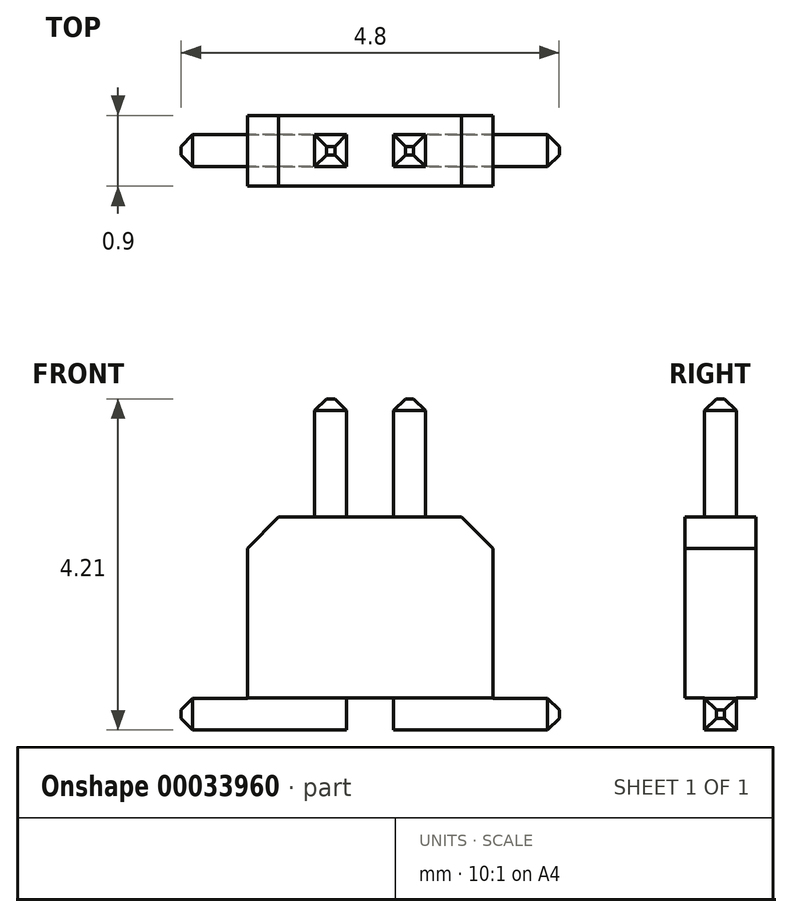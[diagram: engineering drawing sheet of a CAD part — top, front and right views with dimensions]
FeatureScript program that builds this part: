
annotation { "Feature Type Name" : "Feature", "Feature Type Description" : "" }
export const myFeature = defineFeature(function(context is Context, id is Id, definition is map)
    precondition{}
    {
        {
            var Q0;
            Q0=qCreatedBy(makeId("Top.planeOp"),FACE);
            var sketch = newSketch(context, id + "F0", { "sketchPlane" : qUnion([Q0])});
            skLineSegment(sketch, "E0.rect.bottom", {"start": v(-1.56, 0.45) * mm, "end": v(1.56, 0.45) * mm});
            skLineSegment(sketch, "E0.rect.top", {"start": v(-1.56, -0.45) * mm, "end": v(1.56, -0.45) * mm});
            skLineSegment(sketch, "E0.rect.left", {"start": v(-1.56, 0.45) * mm, "end": v(-1.56, -0.45) * mm});
            skLineSegment(sketch, "E0.rect.right", {"start": v(1.56, 0.45) * mm, "end": v(1.56, -0.45) * mm});
            skPoint(sketch, "E0.rect.middle", {"position": v(0, 0) * mm});
            skSolve(sketch);
        }
        {
            var Q0;
            Q0 = qSketchRegion(id + "F0", true);
            extrude(context, id + "F1", {"entities" : qUnion([Q0]), "depth" : 2.3 * mm});
        }
        {
            var Q0;
            Q0=makeQuery(id+"F1.opExtrude","CAP_FACE",FACE,{"disambiguationData":[OSD([sQuery(id+"F0.wireOp",EDGE,"E0.rect.bottom"),sQuery(id+"F0.wireOp",EDGE,"E0.rect.top"),sQuery(id+"F0.wireOp",EDGE,"E0.rect.left"),sQuery(id+"F0.wireOp",EDGE,"E0.rect.right")])],"isStart":false});
            var sketch = newSketch(context, id + "F2", { "sketchPlane" : qUnion([Q0])});
            skLineSegment(sketch, "E1.rect.bottom", {"start": v(-0.7, -0.2) * mm, "end": v(-0.3, -0.2) * mm});
            skLineSegment(sketch, "E1.rect.top", {"start": v(-0.7, 0.2) * mm, "end": v(-0.3, 0.2) * mm});
            skLineSegment(sketch, "E1.rect.left", {"start": v(-0.7, -0.2) * mm, "end": v(-0.7, 0.2) * mm});
            skLineSegment(sketch, "E1.rect.right", {"start": v(-0.3, -0.2) * mm, "end": v(-0.3, 0.2) * mm});
            skPoint(sketch, "E1.rect.middle", {"position": v(-0.5, 0) * mm});
            skLineSegment(sketch, "E2.rect.bottom", {"start": v(0.7, 0.2) * mm, "end": v(0.3, 0.2) * mm});
            skLineSegment(sketch, "E2.rect.top", {"start": v(0.7, -0.2) * mm, "end": v(0.3, -0.2) * mm});
            skLineSegment(sketch, "E2.rect.left", {"start": v(0.7, 0.2) * mm, "end": v(0.7, -0.2) * mm});
            skLineSegment(sketch, "E2.rect.right", {"start": v(0.3, 0.2) * mm, "end": v(0.3, -0.2) * mm});
            skPoint(sketch, "E2.rect.middle", {"position": v(0.5, 0) * mm});
            skSolve(sketch);
        }
        {
            var Q0;
            Q0 = qSketchRegion(id + "F2", true);
            extrude(context, id + "F3", {"entities" : qUnion([Q0]), "operationType" : NewBodyOperationType.ADD, "depth" : 1.5 * mm, "hasSecondDirection" : true, "secondDirectionOppositeDirection" : true, "secondDirectionDepth" : 2.7 * mm});
        }
        {
            var Q0;
            {var subQ0=sQuery(id+"F2.wireOp",EDGE,"E1.rect.left");Q0=makeQuery(id+"F3.boolean.opBoolean","SPLIT",FACE,{"disambiguationData":[TD([makeQuery(id+"F1.opExtrude","CAP_FACE",FACE,{"disambiguationData":[OSD([sQuery(id+"F0.wireOp",EDGE,"E0.rect.bottom"),sQuery(id+"F0.wireOp",EDGE,"E0.rect.top"),sQuery(id+"F0.wireOp",EDGE,"E0.rect.left"),sQuery(id+"F0.wireOp",EDGE,"E0.rect.right")])],"isStart":true})])],"derivedFrom":makeQuery(id+"F3.opExtrude","SWEPT_FACE",FACE,{"disambiguationData":[OSD([subQ0])]})});}
            var sketch = newSketch(context, id + "F4", { "sketchPlane" : qUnion([Q0])});
            skLineSegment(sketch, "E3.bottom", {"start": v(0.2, -0.41) * mm, "end": v(-0.2, -0.41) * mm});
            skLineSegment(sketch, "E3.top", {"start": v(0.2, 0) * mm, "end": v(-0.2, 0) * mm});
            skLineSegment(sketch, "E3.left", {"start": v(0.2, -0.41) * mm, "end": v(0.2, 0) * mm});
            skLineSegment(sketch, "E3.right", {"start": v(-0.2, -0.41) * mm, "end": v(-0.2, 0) * mm});
            skSolve(sketch);
        }
        {
            var Q0;
            Q0 = qSketchRegion(id + "F4", true);
            extrude(context, id + "F5", {"entities" : qUnion([Q0]), "operationType" : NewBodyOperationType.ADD, "depth" : 1.7 * mm});
        }
        {
            var Q0;
            {var subQ0=sQuery(id+"F2.wireOp",EDGE,"E2.rect.left");Q0=makeQuery(id+"F3.boolean.opBoolean","SPLIT",FACE,{"disambiguationData":[TD([makeQuery(id+"F1.opExtrude","CAP_FACE",FACE,{"disambiguationData":[OSD([sQuery(id+"F0.wireOp",EDGE,"E0.rect.bottom"),sQuery(id+"F0.wireOp",EDGE,"E0.rect.top"),sQuery(id+"F0.wireOp",EDGE,"E0.rect.left"),sQuery(id+"F0.wireOp",EDGE,"E0.rect.right")])],"isStart":true})])],"derivedFrom":makeQuery(id+"F3.opExtrude","SWEPT_FACE",FACE,{"disambiguationData":[OSD([subQ0])]})});}
            var sketch = newSketch(context, id + "F6", { "sketchPlane" : qUnion([Q0])});
            skLineSegment(sketch, "E4.bottom", {"start": v(0.2, -0.41) * mm, "end": v(-0.2, -0.41) * mm});
            skLineSegment(sketch, "E4.top", {"start": v(0.2, 0) * mm, "end": v(-0.2, 0) * mm});
            skLineSegment(sketch, "E4.left", {"start": v(0.2, -0.41) * mm, "end": v(0.2, 0) * mm});
            skLineSegment(sketch, "E4.right", {"start": v(-0.2, -0.41) * mm, "end": v(-0.2, 0) * mm});
            skSolve(sketch);
        }
        {
            var Q0;
            Q0 = qSketchRegion(id + "F6", true);
            extrude(context, id + "F7", {"entities" : qUnion([Q0]), "operationType" : NewBodyOperationType.ADD, "depth" : 1.7 * mm});
        }
        {
            var Q0;
            Q0=makeQuery(id+"F1.opExtrude","CAP_EDGE",EDGE,{"disambiguationData":[OSD([sQuery(id+"F0.wireOp",EDGE,"E0.rect.right")])],"isStart":false});
            var Q1;
            Q1=makeQuery(id+"F1.opExtrude","CAP_EDGE",EDGE,{"disambiguationData":[OSD([sQuery(id+"F0.wireOp",EDGE,"E0.rect.left")])],"isStart":false});
            chamfer(context, id + "F8", {"entities" : qUnion([Q0, Q1]), "width" : .4 * mm, "tangentPropagation" : true});
        }
        {
            var Q0;
            Q0=makeQuery(id+"F3.opExtrude","CAP_EDGE",EDGE,{"disambiguationData":[OSD([sQuery(id+"F2.wireOp",EDGE,"E1.rect.top")])],"isStart":false});
            var Q1;
            Q1=makeQuery(id+"F3.opExtrude","CAP_EDGE",EDGE,{"disambiguationData":[OSD([sQuery(id+"F2.wireOp",EDGE,"E2.rect.bottom")])],"isStart":false});
            var Q2;
            Q2=makeQuery(id+"F3.opExtrude","CAP_EDGE",EDGE,{"disambiguationData":[OSD([sQuery(id+"F2.wireOp",EDGE,"E2.rect.left")])],"isStart":false});
            var Q3;
            Q3=makeQuery(id+"F3.opExtrude","CAP_EDGE",EDGE,{"disambiguationData":[OSD([sQuery(id+"F2.wireOp",EDGE,"E2.rect.top")])],"isStart":false});
            var Q4;
            Q4=makeQuery(id+"F3.opExtrude","CAP_EDGE",EDGE,{"disambiguationData":[OSD([sQuery(id+"F2.wireOp",EDGE,"E2.rect.right")])],"isStart":false});
            var Q5;
            Q5=makeQuery(id+"F3.opExtrude","CAP_EDGE",EDGE,{"disambiguationData":[OSD([sQuery(id+"F2.wireOp",EDGE,"E1.rect.right")])],"isStart":false});
            var Q6;
            Q6=makeQuery(id+"F3.opExtrude","CAP_EDGE",EDGE,{"disambiguationData":[OSD([sQuery(id+"F2.wireOp",EDGE,"E1.rect.bottom")])],"isStart":false});
            var Q7;
            Q7=makeQuery(id+"F3.opExtrude","CAP_EDGE",EDGE,{"disambiguationData":[OSD([sQuery(id+"F2.wireOp",EDGE,"E1.rect.left")])],"isStart":false});
            var Q8;
            Q8=makeQuery(id+"F5.opExtrude","CAP_EDGE",EDGE,{"disambiguationData":[OSD([sQuery(id+"F4.wireOp",EDGE,"E3.top")])],"isStart":false});
            var Q9;
            Q9=makeQuery(id+"F5.opExtrude","CAP_EDGE",EDGE,{"disambiguationData":[OSD([sQuery(id+"F4.wireOp",EDGE,"E3.right")])],"isStart":false});
            var Q10;
            Q10=makeQuery(id+"F5.opExtrude","CAP_EDGE",EDGE,{"disambiguationData":[OSD([sQuery(id+"F4.wireOp",EDGE,"E3.bottom")])],"isStart":false});
            var Q11;
            Q11=makeQuery(id+"F5.opExtrude","CAP_EDGE",EDGE,{"disambiguationData":[OSD([sQuery(id+"F4.wireOp",EDGE,"E3.left")])],"isStart":false});
            var Q12;
            Q12=makeQuery(id+"F7.opExtrude","CAP_EDGE",EDGE,{"disambiguationData":[OSD([sQuery(id+"F6.wireOp",EDGE,"E4.top")])],"isStart":false});
            var Q13;
            Q13=makeQuery(id+"F7.opExtrude","CAP_EDGE",EDGE,{"disambiguationData":[OSD([sQuery(id+"F6.wireOp",EDGE,"E4.left")])],"isStart":false});
            var Q14;
            Q14=makeQuery(id+"F7.opExtrude","CAP_EDGE",EDGE,{"disambiguationData":[OSD([sQuery(id+"F6.wireOp",EDGE,"E4.bottom")])],"isStart":false});
            var Q15;
            Q15=makeQuery(id+"F7.opExtrude","CAP_EDGE",EDGE,{"disambiguationData":[OSD([sQuery(id+"F6.wireOp",EDGE,"E4.right")])],"isStart":false});
            chamfer(context, id + "F9", {"entities" : qUnion([Q0, Q1, Q2, Q3, Q4, Q5, Q6, Q7, Q8, Q9, Q10, Q11, Q12, Q13, Q14, Q15]), "width" : .15 * mm, "tangentPropagation" : true});
        }
    });
